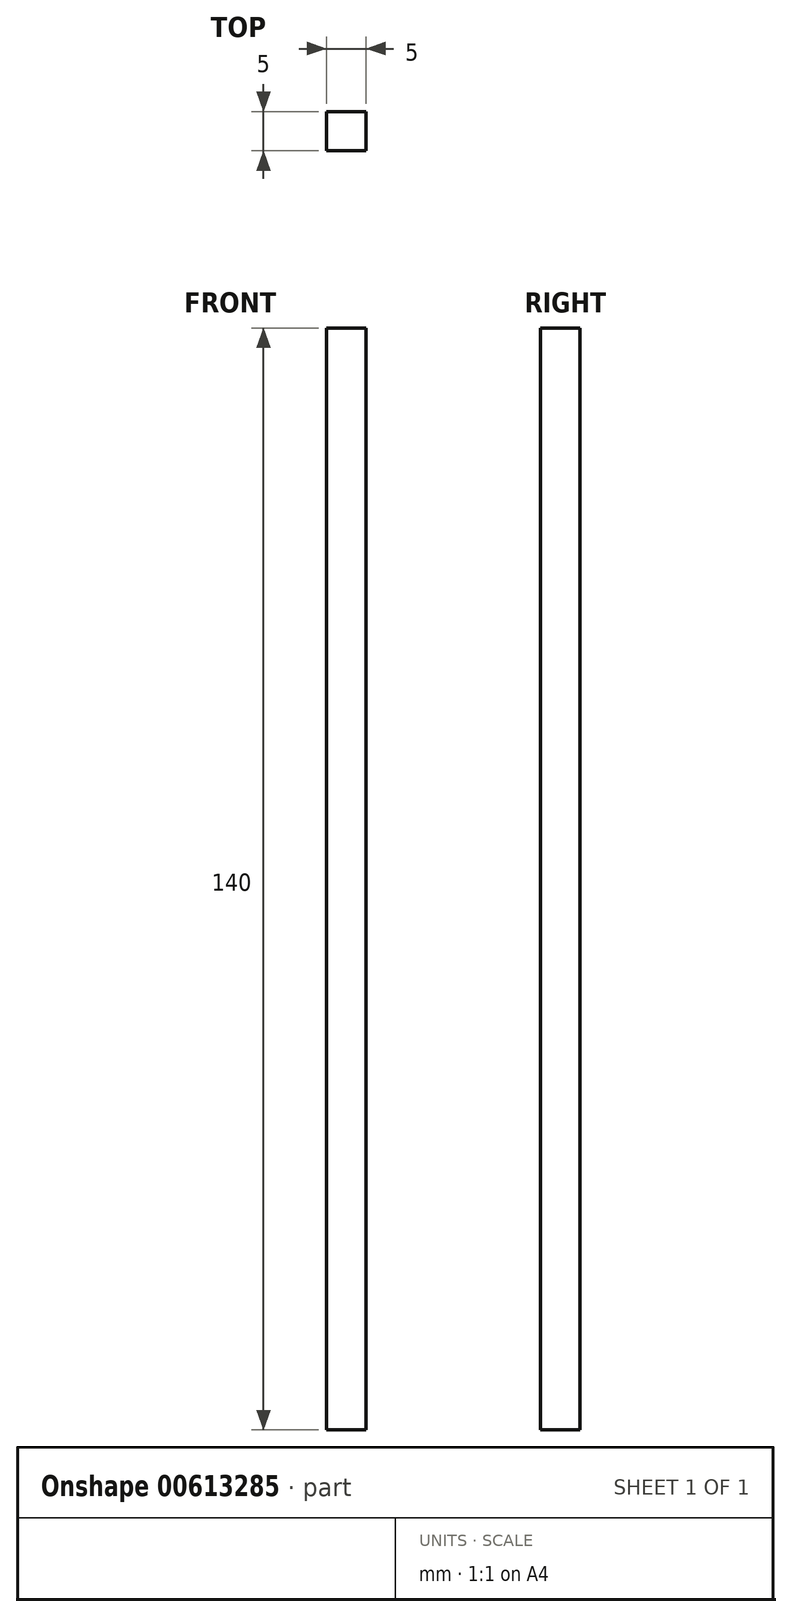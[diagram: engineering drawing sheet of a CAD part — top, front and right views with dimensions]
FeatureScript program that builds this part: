
annotation { "Feature Type Name" : "Feature", "Feature Type Description" : "" }
export const myFeature = defineFeature(function(context is Context, id is Id, definition is map)
    precondition{}
    {
        {
            var Q0;
            Q0=qCreatedBy(makeId("Top.planeOp"),FACE);
            var sketch = newSketch(context, id + "F0", { "sketchPlane" : qUnion([Q0])});
            skLineSegment(sketch, "E0.bottom", {"start": v(2.5, -2.5) * mm, "end": v(-2.5, -2.5) * mm});
            skLineSegment(sketch, "E0.top", {"start": v(2.5, 2.5) * mm, "end": v(-2.5, 2.5) * mm});
            skLineSegment(sketch, "E0.left", {"start": v(2.5, -2.5) * mm, "end": v(2.5, 2.5) * mm});
            skLineSegment(sketch, "E0.right", {"start": v(-2.5, -2.5) * mm, "end": v(-2.5, 2.5) * mm});
            skPoint(sketch, "E0.middle", {"position": v(0, 0) * mm});
            skSolve(sketch);
        }
        {
            var Q0;
            Q0=makeQuery(id+"F0.imprint","IMPRINT",FACE,{"disambiguationData":[TD([[makeQuery(id+"F0.imprint","IMPRINT",EDGE,{"derivedFrom":sQuery(id+"F0.wireOp",EDGE,"E0.bottom")}),-1.0]])]});
            extrude(context, id + "F1", {"entities" : qUnion([Q0]), "depth" : 140 * mm, "offsetDistance" : 25 * mm});
        }
    });
